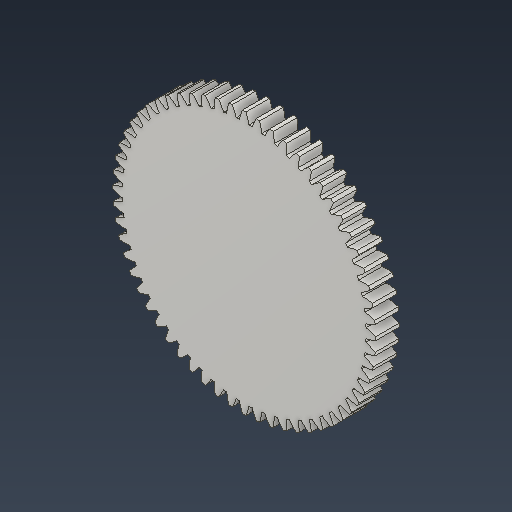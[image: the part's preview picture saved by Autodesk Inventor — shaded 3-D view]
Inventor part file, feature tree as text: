
AUTODESK INVENTOR PART (.ipt)
format: ipt  version: 2021 (Build 250183000, 183)  size: 384,000 bytes
history: native  units: mm (DEFAULTED — no unit token found)
features: plane x3, other x3, sketch x2, extrude x1
ambient origin geometry x8: Origin, YZ Plane, XZ Plane, XY Plane, X Axis, Y Axis, Z Axis, Center Point
bodies: Solid1 (feature_tree)
feature tree (9):
  extrude  "Extrusion1"  Depth=0.5mm TaperAngle=0.0deg
  plane  "Work Plane2"
  plane  "Work Plane8"
  plane  "Work Plane9"
  other  "Engrenagem reta"
  sketch  "Sketch1"  dims[d0=5.575177mm d1=0.5mm d2=0.0mm]
  sketch  "Sketch2"  dims[d3=5.4mm d4=10.0mm d5=0.0mm d16=3.597588mm d17=0.0mm d34=0.523599mm d39=0.0mm d41=0.0mm d43=3.597588mm d46=3.597588mm d47=0.0mm d48=0.0mm]
  other  "Srf1"
  other  "Diâmetro do flanco"
